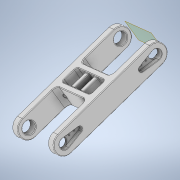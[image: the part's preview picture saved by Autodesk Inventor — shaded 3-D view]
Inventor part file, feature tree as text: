
AUTODESK INVENTOR PART (.ipt)
format: ipt  version: 2020.3 (Build 243373000, 373)  size: 557,568 bytes
history: native  units: mm
features: fillet x14, sketch x8, extrude x7, hole x3, plane x1, chamfer x1
ambient origin geometry x8: Origin, YZ Plane, XZ Plane, XY Plane, X Axis, Y Axis, Z Axis, Center Point
bodies: Solid1 (feature_tree)
feature tree (34):
  extrude  "Extrusion1"  Depth=34.0mm
  sketch  "Sketch2"  dims[d11=20.0mm d12=15.0mm d13=0.0mm d14=3.0mm d15=6.0mm d16=4.0mm d19=6.0mm d20=0.0mm]
  extrude  "Extrusion2"  Depth=15.0mm TaperAngle=0.0deg
  fillet  "Fillet1"  Radius=3.0mm
  fillet  "Fillet2"  Radius=6.0mm
  fillet  "Fillet3"  Radius=4.0mm
  fillet  "Fillet4"  Radius=6.0mm
  sketch  "Sketch5"  dims[d30=35.0mm d31=35.0mm]
  extrude  "Extrusion4"  Depth=35.0mm
  extrude  "Extrusion5"  Depth=12.1mm
  hole  "Hole7"  [1 undecoded]
  extrude  "Extrusion6"  Depth=1.0mm TaperAngle=0.0deg
  extrude  "Extrusion7"  Depth=12.1mm
  hole  "Hole5"  [1 undecoded]
  fillet  "Fillet13"  Radius=0.5mm
  fillet  "Fillet11"  Radius=2.0mm
  fillet  "Fillet9"  Radius=0.2mm
  fillet  "Fillet15"  Radius=3.5mm
  fillet  "Fillet12"  Radius=0.5mm
  hole  "Hole6"  [1 undecoded]
  fillet  "Fillet14"  Radius=0.5mm
  fillet  "Fillet16"  Radius=0.3mm
  fillet  "Fillet17"  Radius=2.0mm
  plane  "Work Plane1"
  extrude  "Extrusion8"  Depth=2.0mm
  chamfer  "Chamfer1"  Distance=2.0mm
  fillet  "Fillet20"  Radius=35.0mm
  fillet  "Fillet21"  Radius=7.0mm
  sketch  "Sketch1"  dims[d2=6.0mm d8=34.0mm]
  sketch  "Sketch6"  dims[d53=3.7mm d54=12.1mm]
  sketch  "Sketch12"  dims[d61=4.0mm d62=0.0mm d63=3.5mm d64=0.0mm]
  sketch  "Sketch13"  dims[d68=1.0mm d69=0.0mm d70=1.0mm d71=0.0mm]
  sketch  "Sketch14"  dims[d72=1.0mm d76=12.1mm]
  sketch  "Sketch15"  dims[d89=7.2mm d97=3.0mm d98=3.0mm d99=6.0mm d100=4.0mm d101=2.0mm d102=90.0deg d103=5.0mm d104=20.594885mm d105=0.5mm d107=2.0mm d108=0.2mm d109=3.5mm d110=8.7mm d111=6.0mm d112=4.0mm d113=2.0mm d114=90.0deg d115=5.0mm d116=20.594885mm d117=0.5mm d118=0.5mm d119=0.5mm d120=0.3mm d121=2.0mm d122=2.0mm d123=2.0mm d124=1.0mm d125=6.0mm d126=4.0mm d127=2.0mm d128=90.0deg d129=10.0mm d130=20.594885mm d131=35.0mm d132=7.0mm d133=7.0mm d134=0.0mm d138=0.2mm d139=0.8mm d140=45.0deg d141=1.0mm d142=2.0mm]
note: 3 required parameter values undecoded (feature->parameter linkage not recoverable at this tier; creation-order binding heuristic only, values carry confidence <= 0.55)
